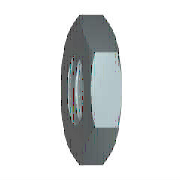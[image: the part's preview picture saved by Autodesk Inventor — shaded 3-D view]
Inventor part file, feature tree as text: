
AUTODESK INVENTOR PART (.ipt)
format: ipt  version: 2020 (Build 240168000, 168)  size: 166,912 bytes
history: native  units: mm (DEFAULTED — no unit token found)
features: sketch x3, extrude x1, chamfer x1, hole x1, other x1, plane x1
ambient origin geometry x7: Origin, YZ Plane, XZ Plane, X Axis, Y Axis, Z Axis, Center Point
bodies: Solid1 (feature_tree)
feature tree (8):
  extrude  "Körper"  Depth=1.8mm
  chamfer  "Fase1"  Angle=30.0deg  [1 undecoded]
  hole  "Gewinde"  [1 undecoded]
  other  "Work Axis1"
  plane  "Work Plane1"
  sketch  "Skizze1"  dims[d0=6.350853mm d1=1.8mm]
  sketch  "Skizze2"  dims[d2=0.0mm]
  sketch  "Skizze3"  dims[d3=30.0deg d4=30.0deg d5=4.6mm d6=4.6mm d7=90.0deg d25=2.459mm d26=6.0mm d27=4.0mm d28=2.0mm d29=14.3117mm d30=8.0mm d31=20.594885mm d8=0.270633mm d9=30.0deg d10=0.270633mm d11=30.0deg d13=0.0mm d14=0.0mm d39=0.0mm d40=0.270633mm d41=0.270633mm d42=0.0mm]
note: 2 required parameter values undecoded (feature->parameter linkage not recoverable at this tier; creation-order binding heuristic only, values carry confidence <= 0.55)
